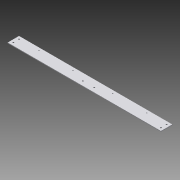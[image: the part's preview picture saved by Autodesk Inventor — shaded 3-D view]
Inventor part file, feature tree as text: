
AUTODESK INVENTOR PART (.ipt)
format: ipt  version: 2015 (Build 190159000, 159)  size: 193,024 bytes
history: native  units: in
note: dims shown in document units (in); Inventor stores cm internally (conversion verified against a paired STEP export)
features: sketch x7, hole x5, extrude x2, chamfer x1
ambient origin geometry x8: Origin, YZ Plane, XZ Plane, XY Plane, X Axis, Y Axis, Z Axis, Center Point
bodies: Solid1 (feature_tree)
feature tree (15):
  extrude  "Extrusion1"  Depth=2.0in
  sketch  "Sketch2"  dims[d2=2.0in d3=0.125in]
  hole  "Hole2"  [1 undecoded]
  hole  "Hole3"  [1 undecoded]
  extrude  "Extrusion3"  Depth=0.5in
  chamfer  "Chamfer1"  Distance=0.75in
  hole  "Hole5"  [1 undecoded]
  hole  "Hole6"  [1 undecoded]
  hole  "Hole7"  [1 undecoded]
  sketch  "Sketch1"  dims[d0=0.125in d1=2.0in]
  sketch  "Sketch3"  dims[d4=27.0in d5=0.0in d9=0.5in]
  sketch  "Sketch4"  dims[d11=0.5in d19=0.5in]
  sketch  "Sketch6"  dims[d20=0.5in]
  sketch  "Sketch8"  dims[d21=0.5in]
  sketch  "Sketch9"  dims[d22=0.5in d23=0.75in d24=0.75in d25=0.5in d26=0.5in d27=0.5in d28=0.5in d29=12.5in d30=12.5in d31=0.25in d32=0.75in d33=0.375in d34=0.25in d35=0.5635in d36=1.0in d37=0.8108in d38=4.0in d39=10.0in d40=10.0in d41=4.0in d42=0.5in d43=0.5in d44=0.5in d45=0.5in d46=0.1875in d47=0.75in d48=0.375in d49=0.25in d50=0.5635in d51=1.0in d52=0.8108in d65=6.0in d66=1.0in d67=6.0in d68=1.0in d69=45.0deg d70=135.0deg d71=1.0in d72=0.0in d73=0.125in d74=0.125in d75=45.0deg d91=0.5in d92=0.5in d93=0.5in d94=0.5in d95=4.0in d96=10.0in d97=17.0in d98=23.0in d99=0.1875in d100=0.75in d101=0.375in d102=0.25in d103=0.5635in d104=1.0in d105=0.8108in d106=8.0in d107=0.25in d108=0.25in d109=8.0in d110=0.375in d111=0.75in d112=0.375in d113=0.25in d114=0.5635in d115=1.0in d116=0.8108in d117=0.5in d118=0.5in d121=0.5in d122=0.5in d123=0.25in d124=0.75in d125=0.375in d126=0.25in d127=0.5635in d128=1.0in d129=0.8108in d130=8.125in d131=9.75in]
note: 5 required parameter values undecoded (feature->parameter linkage not recoverable at this tier; creation-order binding heuristic only, values carry confidence <= 0.55)
